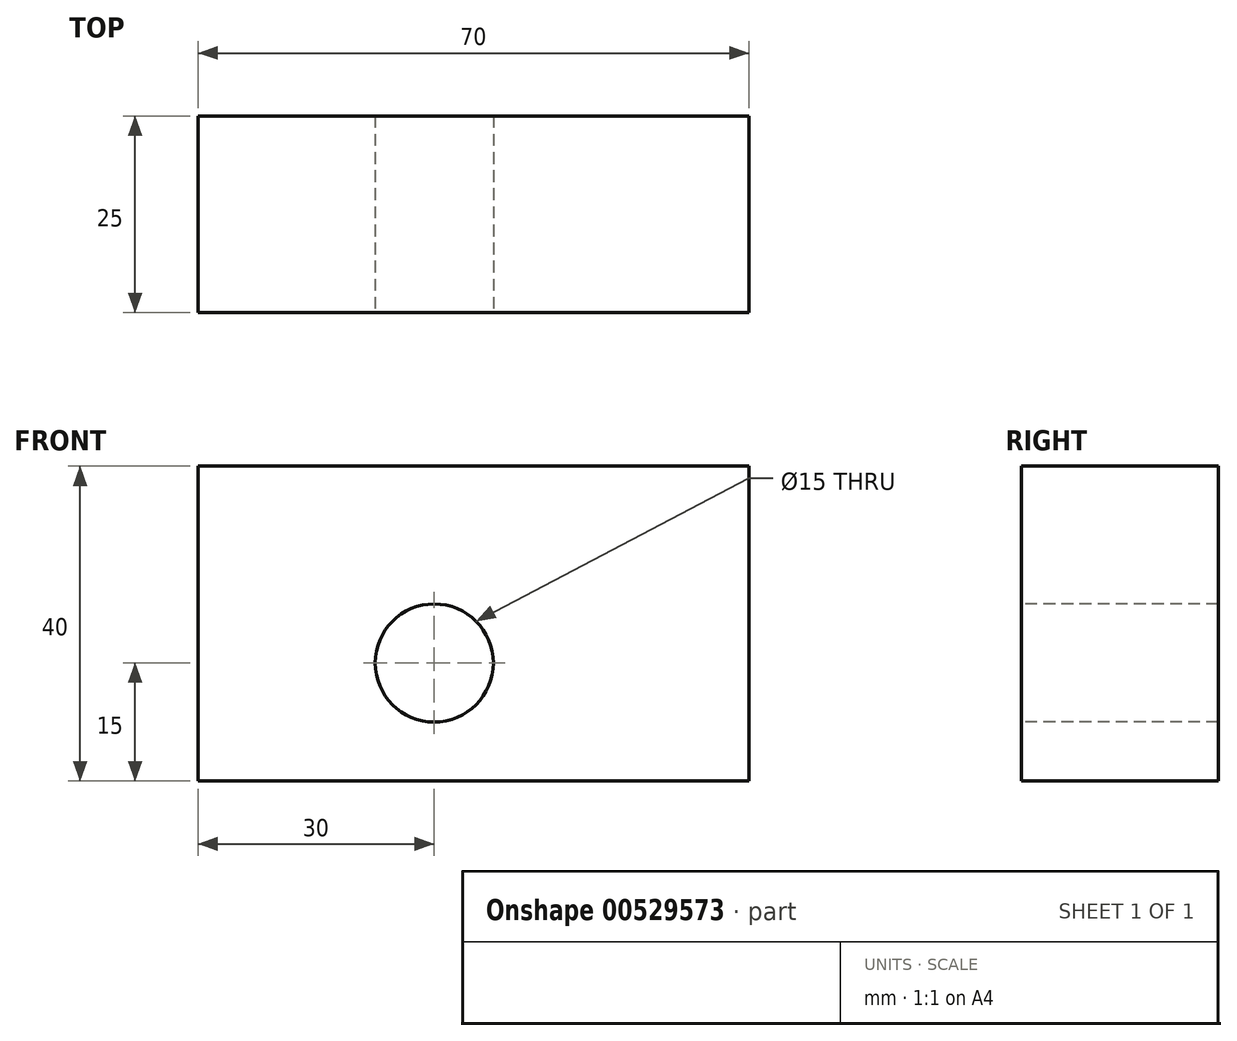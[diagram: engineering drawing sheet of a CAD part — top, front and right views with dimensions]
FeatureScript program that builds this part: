
annotation { "Feature Type Name" : "Feature", "Feature Type Description" : "" }
export const myFeature = defineFeature(function(context is Context, id is Id, definition is map)
    precondition{}
    {
        {
            var Q0;
            Q0=qCreatedBy(makeId("Front.planeOp"),FACE);
            var sketch = newSketch(context, id + "F0", { "sketchPlane" : qUnion([Q0])});
            skLineSegment(sketch, "E0.bottom", {"start": v(0, 0) * mm, "end": v(70, 0) * mm});
            skLineSegment(sketch, "E0.top", {"start": v(0, 40) * mm, "end": v(70, 40) * mm});
            skLineSegment(sketch, "E0.left", {"start": v(0, 0) * mm, "end": v(0, 40) * mm});
            skLineSegment(sketch, "E0.right", {"start": v(70, 0) * mm, "end": v(70, 40) * mm});
            skSolve(sketch);
        }
        {
            var Q0;
            Q0=makeQuery(id+"F0.imprint","IMPRINT",FACE,{"disambiguationData":[TD([[makeQuery(id+"F0.imprint","IMPRINT",EDGE,{"derivedFrom":sQuery(id+"F0.wireOp",EDGE,"E0.bottom")}),1.0]])]});
            extrude(context, id + "F1", {"entities" : qUnion([Q0]), "depth" : 25 * mm, "offsetDistance" : 25 * mm});
        }
        {
            var Q0;
            Q0=makeQuery(id+"F1.opExtrude","CAP_FACE",FACE,{"disambiguationData":[OSD([sQuery(id+"F0.wireOp",EDGE,"E0.bottom"),sQuery(id+"F0.wireOp",EDGE,"E0.top"),sQuery(id+"F0.wireOp",EDGE,"E0.left"),sQuery(id+"F0.wireOp",EDGE,"E0.right")])],"isStart":false});
            var sketch = newSketch(context, id + "F2", { "sketchPlane" : qUnion([Q0])});
            skCircle(sketch, "E1", {"center": v(30, 15) * mm, "radius": 7.5 * mm});
            skSolve(sketch);
        }
        {
            var Q0;
            Q0 = qSketchRegion(id + "F2", true);
            extrude(context, id + "F3", {"entities" : qUnion([Q0]), "operationType" : NewBodyOperationType.REMOVE, "oppositeDirection" : true, "depth" : 25 * mm, "offsetDistance" : 25 * mm});
        }
    });
